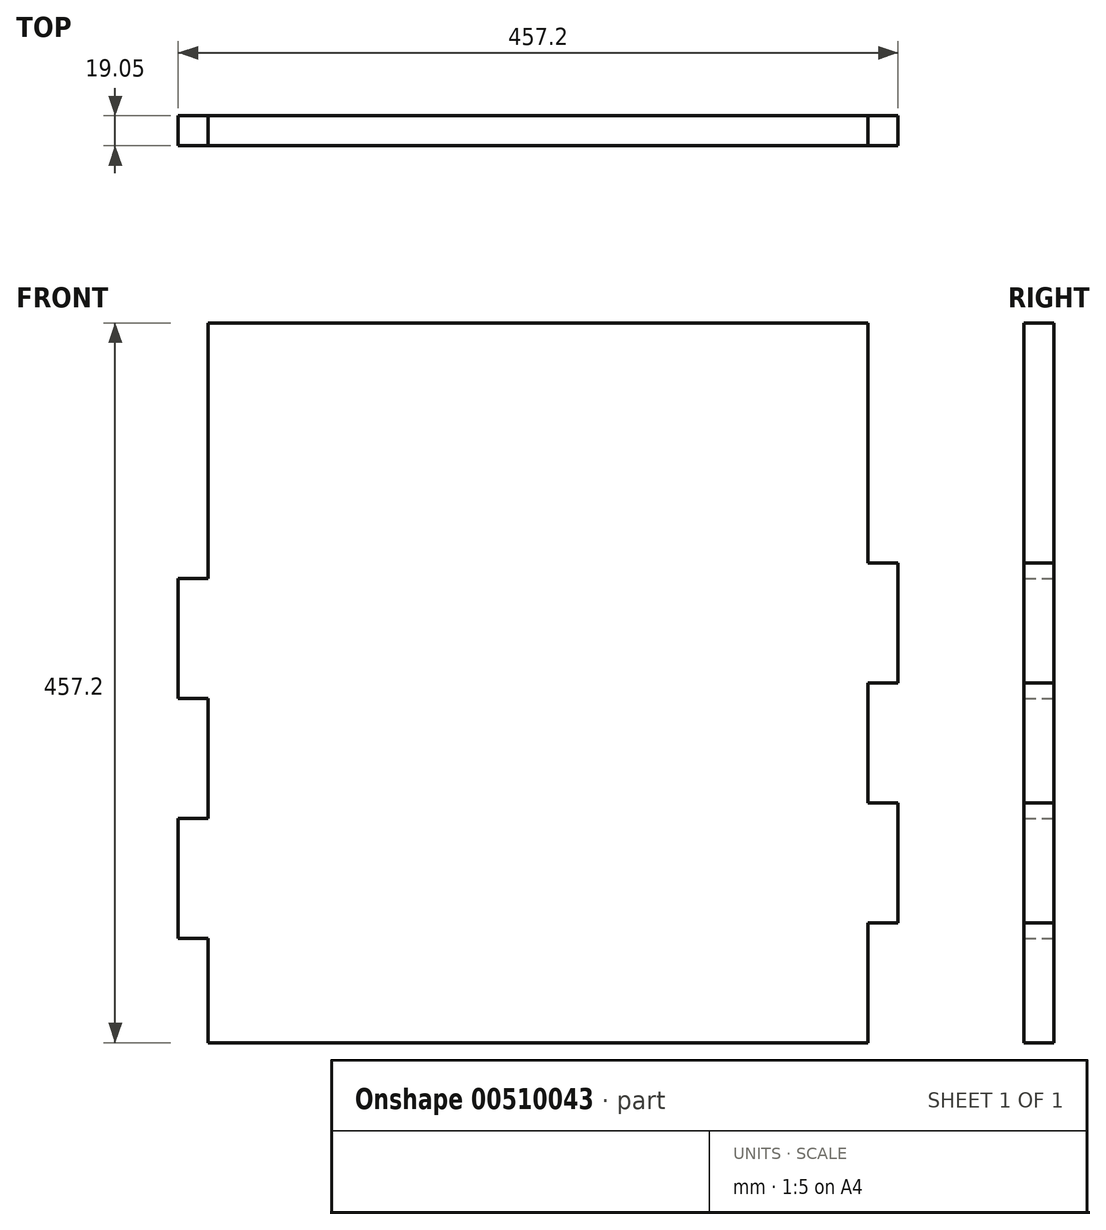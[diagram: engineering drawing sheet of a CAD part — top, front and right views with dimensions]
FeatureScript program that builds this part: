
annotation { "Feature Type Name" : "Feature", "Feature Type Description" : "" }
export const myFeature = defineFeature(function(context is Context, id is Id, definition is map)
    precondition{}
    {
        {
            var Q0;
            Q0=qCreatedBy(makeId("Front.planeOp"),FACE);
            var sketch = newSketch(context, id + "F0", { "sketchPlane" : qUnion([Q0])});
            skLineSegment(sketch, "E0", {"start": v(-338.31, 152.4) * mm, "end": v(-338.31, -304.8) * mm});
            skLineSegment(sketch, "E1", {"start": v(-338.31, -304.8) * mm, "end": v(80.79, -304.8) * mm});
            skLineSegment(sketch, "E2", {"start": v(80.79, -304.8) * mm, "end": v(80.79, 152.4) * mm});
            skLineSegment(sketch, "E3", {"start": v(80.79, 152.4) * mm, "end": v(-338.31, 152.4) * mm});
            skLineSegment(sketch, "E4.bottom", {"start": v(-357.36, -10.01) * mm, "end": v(-338.31, -10.01) * mm});
            skLineSegment(sketch, "E4.top", {"start": v(-357.36, -86.21) * mm, "end": v(-338.31, -86.21) * mm});
            skLineSegment(sketch, "E4.left", {"start": v(-357.36, -10.01) * mm, "end": v(-357.36, -86.21) * mm});
            skLineSegment(sketch, "E4.right", {"start": v(-338.31, -10.01) * mm, "end": v(-338.31, -86.21) * mm});
            skLineSegment(sketch, "E5.bottom", {"start": v(-357.36, -162.41) * mm, "end": v(-338.31, -162.41) * mm});
            skLineSegment(sketch, "E5.top", {"start": v(-357.36, -238.61) * mm, "end": v(-338.31, -238.61) * mm});
            skLineSegment(sketch, "E5.left", {"start": v(-357.36, -162.41) * mm, "end": v(-357.36, -238.61) * mm});
            skLineSegment(sketch, "E5.right", {"start": v(-338.31, -162.41) * mm, "end": v(-338.31, -238.61) * mm});
            skLineSegment(sketch, "E6.bottom", {"start": v(80.79, -304.8) * mm, "end": v(99.84, -304.8) * mm});
            skLineSegment(sketch, "E6.top", {"start": v(80.79, -228.6) * mm, "end": v(99.84, -228.6) * mm});
            skLineSegment(sketch, "E6.left", {"start": v(80.79, -304.8) * mm, "end": v(80.79, -228.6) * mm});
            skLineSegment(sketch, "E7.bottom", {"start": v(99.84, -152.4) * mm, "end": v(80.79, -152.4) * mm});
            skLineSegment(sketch, "E7.top", {"start": v(99.84, -76.2) * mm, "end": v(80.79, -76.2) * mm});
            skLineSegment(sketch, "E7.right", {"start": v(80.79, -152.4) * mm, "end": v(80.79, -76.2) * mm});
            skLineSegment(sketch, "E8.bottom", {"start": v(99.84, 0) * mm, "end": v(80.79, 0) * mm});
            skLineSegment(sketch, "E8.right", {"start": v(80.79, 0) * mm, "end": v(80.79, 76.2) * mm});
            skLineSegment(sketch, "E9.left", {"start": v(99.84, 0) * mm, "end": v(99.84, -76.2) * mm});
            skLineSegment(sketch, "E9.right", {"start": v(80.79, 0) * mm, "end": v(80.79, -76.2) * mm});
            skLineSegment(sketch, "E10.top", {"start": v(99.84, -228.6) * mm, "end": v(80.79, -228.6) * mm});
            skLineSegment(sketch, "E10.left", {"start": v(99.84, -152.4) * mm, "end": v(99.84, -228.6) * mm});
            skLineSegment(sketch, "E10.right", {"start": v(80.79, -152.4) * mm, "end": v(80.79, -228.6) * mm});
            skSolve(sketch);
        }
        {
            var Q0;
            Q0 = qSketchRegion(id + "F0", true);
            extrude(context, id + "F1", {"entities" : qUnion([Q0]), "depth" : 19.05 * mm, "offsetDistance" : 25.4 * mm});
        }
    });
